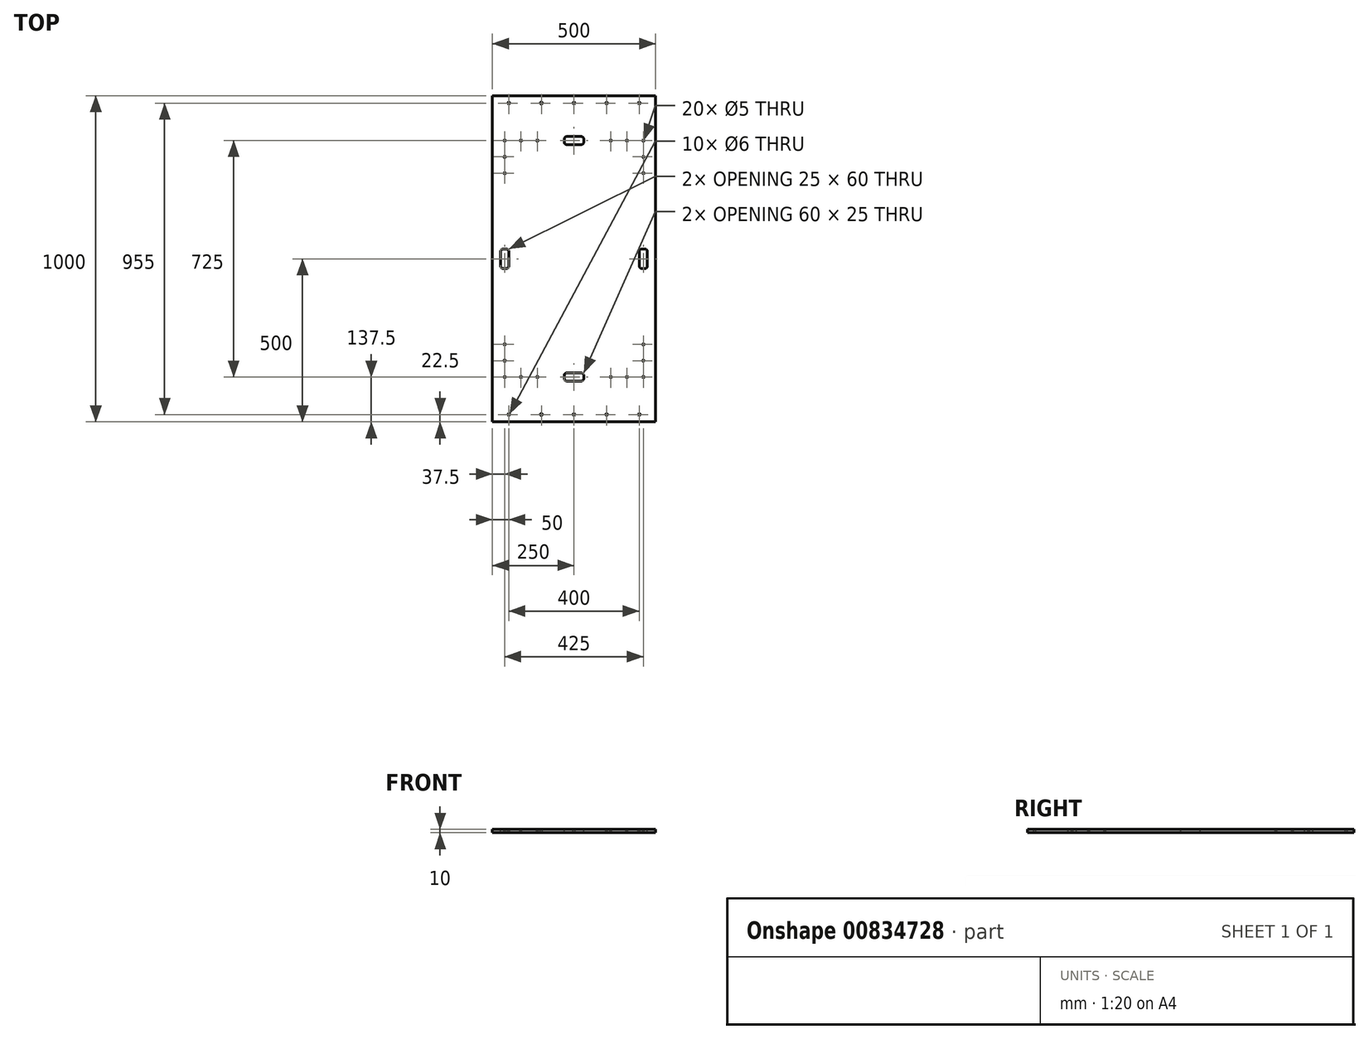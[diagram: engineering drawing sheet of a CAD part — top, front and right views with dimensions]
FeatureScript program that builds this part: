
annotation { "Feature Type Name" : "Feature", "Feature Type Description" : "" }
export const myFeature = defineFeature(function(context is Context, id is Id, definition is map)
    precondition{}
    {
        {
            var Q0;
            Q0=qCreatedBy(makeId("Top.planeOp"),FACE);
            var sketch = newSketch(context, id + "F0", { "sketchPlane" : qUnion([Q0])});
            skLineSegment(sketch, "E0.bottom", {"start": v(-250, 500) * mm, "end": v(250, 500) * mm});
            skLineSegment(sketch, "E0.top", {"start": v(-250, -500) * mm, "end": v(250, -500) * mm});
            skLineSegment(sketch, "E0.left", {"start": v(-250, 500) * mm, "end": v(-250, -500) * mm});
            skLineSegment(sketch, "E0.right", {"start": v(250, 500) * mm, "end": v(250, -500) * mm});
            skPoint(sketch, "E0.middle", {"position": v(0, 0) * mm});
            skSolve(sketch);
        }
        {
            var Q0;
            Q0=makeQuery(id+"F0.imprint","IMPRINT",FACE,{"disambiguationData":[TD([[makeQuery(id+"F0.imprint","IMPRINT",EDGE,{"derivedFrom":sQuery(id+"F0.wireOp",EDGE,"E0.bottom")}),-1.0]])]});
            extrude(context, id + "F1", {"entities" : qUnion([Q0]), "depth" : 10 * mm, "offsetDistance" : 25 * mm});
        }
        {
            var Q0;
            Q0=makeQuery(id+"F1.opExtrude","CAP_FACE",FACE,{"disambiguationData":[OSD([sQuery(id+"F0.wireOp",EDGE,"E0.bottom"),sQuery(id+"F0.wireOp",EDGE,"E0.top"),sQuery(id+"F0.wireOp",EDGE,"E0.left"),sQuery(id+"F0.wireOp",EDGE,"E0.right")])],"isStart":false});
            var sketch = newSketch(context, id + "F2", { "sketchPlane" : qUnion([Q0])});
            skLineSegment(sketch, "E1", {"start": v(250, 0) * mm, "end": v(-250, 0) * mm});
            skLineSegment(sketch, "E2", {"start": v(0, 500) * mm, "end": v(0, -500) * mm});
            skLineSegment(sketch, "E3", {"start": v(250, 477.5) * mm, "end": v(-250, 477.5) * mm});
            skLineSegment(sketch, "E4", {"start": v(250, -477.5) * mm, "end": v(-250, -477.5) * mm});
            skPoint(sketch, "E5", {"position": v(-200, 477.5) * mm});
            skPoint(sketch, "E6", {"position": v(-100, 477.5) * mm});
            skPoint(sketch, "E7", {"position": v(0, 477.5) * mm});
            skPoint(sketch, "E8", {"position": v(100, 477.5) * mm});
            skPoint(sketch, "E9", {"position": v(200, 477.5) * mm});
            skPoint(sketch, "E10", {"position": v(-200, -477.5) * mm});
            skPoint(sketch, "E11", {"position": v(-100, -477.5) * mm});
            skPoint(sketch, "E12", {"position": v(0, -477.5) * mm});
            skPoint(sketch, "E13", {"position": v(100, -477.5) * mm});
            skPoint(sketch, "E14", {"position": v(200, -477.5) * mm});
            skPoint(sketch, "E15", {"position": v(-212.5, 0) * mm});
            skPoint(sketch, "E16", {"position": v(212.5, 0) * mm});
            skLineSegment(sketch, "E17.bottom", {"start": v(200, -30) * mm, "end": v(225, -30) * mm});
            skLineSegment(sketch, "E17.top", {"start": v(200, 30) * mm, "end": v(225, 30) * mm});
            skLineSegment(sketch, "E17.left", {"start": v(200, -30) * mm, "end": v(200, 30) * mm});
            skLineSegment(sketch, "E17.right", {"start": v(225, -30) * mm, "end": v(225, 30) * mm});
            skLineSegment(sketch, "E18.bottom", {"start": v(-225, -30) * mm, "end": v(-200, -30) * mm});
            skLineSegment(sketch, "E18.top", {"start": v(-225, 30) * mm, "end": v(-200, 30) * mm});
            skLineSegment(sketch, "E18.left", {"start": v(-225, -30) * mm, "end": v(-225, 30) * mm});
            skLineSegment(sketch, "E18.right", {"start": v(-200, -30) * mm, "end": v(-200, 30) * mm});
            skSolve(sketch);
        }
        {
            var Q0;
            Q0=sQuery(id+"F2.wireOp",VERTEX,"E9");
            var Q1;
            Q1=sQuery(id+"F2.wireOp",VERTEX,"E8");
            var Q2;
            Q2=sQuery(id+"F2.wireOp",VERTEX,"E7");
            var Q3;
            Q3=sQuery(id+"F2.wireOp",VERTEX,"E6");
            var Q4;
            Q4=sQuery(id+"F2.wireOp",VERTEX,"E5");
            var Q5;
            Q5=sQuery(id+"F2.wireOp",VERTEX,"E14");
            var Q6;
            Q6=sQuery(id+"F2.wireOp",VERTEX,"E13");
            var Q7;
            Q7=sQuery(id+"F2.wireOp",VERTEX,"E12");
            var Q8;
            Q8=sQuery(id+"F2.wireOp",VERTEX,"E11");
            var Q9;
            Q9=sQuery(id+"F2.wireOp",VERTEX,"E10");
            var Q10;
            Q10=makeQuery(id+"F1.opExtrude","SWEPT_BODY",BODY,{"disambiguationData":[OSD([sQuery(id+"F0.wireOp",EDGE,"E0.bottom"),sQuery(id+"F0.wireOp",EDGE,"E0.top"),sQuery(id+"F0.wireOp",EDGE,"E0.left"),sQuery(id+"F0.wireOp",EDGE,"E0.right")])]});
            hole(context, id + "F3", {"style" : HoleStyle.SIMPLE, "endStyle" : HoleEndStyle.THROUGH, "holeDiameter" : 6 * mm, "majorDiameter" : 5 * mm, "isTappedThrough" : true, "tappedDepth" : 12 * mm, "tapClearance" : 3, "locations" : qUnion([Q0, Q1, Q2, Q3, Q4, Q5, Q6, Q7, Q8, Q9]), "scope" : qUnion([Q10])});
        }
        {
            var Q0;
            Q0 = qSketchRegion(id + "F2", true);
            extrude(context, id + "F4", {"entities" : qUnion([Q0]), "operationType" : NewBodyOperationType.REMOVE, "oppositeDirection" : true, "depth" : 25 * mm, "offsetDistance" : 25 * mm});
        }
        {
            var Q0;
            Q0=makeQuery(id+"F1.opExtrude","CAP_FACE",FACE,{"disambiguationData":[OSD([sQuery(id+"F0.wireOp",EDGE,"E0.bottom"),sQuery(id+"F0.wireOp",EDGE,"E0.top"),sQuery(id+"F0.wireOp",EDGE,"E0.left"),sQuery(id+"F0.wireOp",EDGE,"E0.right")])],"isStart":false});
            var sketch = newSketch(context, id + "F5", { "sketchPlane" : qUnion([Q0])});
            skLineSegment(sketch, "E19", {"start": v(0, -500) * mm, "end": v(0, 500) * mm});
            skPoint(sketch, "E20", {"position": v(0, -362.5) * mm});
            skPoint(sketch, "E21", {"position": v(0, 362.5) * mm});
            skLineSegment(sketch, "E22.bottom", {"start": v(30, 375) * mm, "end": v(-30, 375) * mm});
            skLineSegment(sketch, "E22.top", {"start": v(30, 350) * mm, "end": v(-30, 350) * mm});
            skLineSegment(sketch, "E22.left", {"start": v(30, 375) * mm, "end": v(30, 350) * mm});
            skLineSegment(sketch, "E22.right", {"start": v(-30, 375) * mm, "end": v(-30, 350) * mm});
            skLineSegment(sketch, "E23.bottom", {"start": v(30, -350) * mm, "end": v(-30, -350) * mm});
            skLineSegment(sketch, "E23.top", {"start": v(30, -375) * mm, "end": v(-30, -375) * mm});
            skLineSegment(sketch, "E23.left", {"start": v(30, -350) * mm, "end": v(30, -375) * mm});
            skLineSegment(sketch, "E23.right", {"start": v(-30, -350) * mm, "end": v(-30, -375) * mm});
            skPoint(sketch, "E24", {"position": v(0, 0) * mm});
            skSolve(sketch);
        }
        {
            var Q0;
            Q0 = qSketchRegion(id + "F5", true);
            extrude(context, id + "F6", {"entities" : qUnion([Q0]), "operationType" : NewBodyOperationType.REMOVE, "oppositeDirection" : true, "depth" : 25 * mm, "offsetDistance" : 25 * mm});
        }
        {
            var Q0;
            Q0=makeQuery(id+"F6.boolean.opBoolean","COPY",EDGE,{"derivedFrom":makeQuery(id+"F6.opExtrude","SWEPT_EDGE",EDGE,{"disambiguationData":[OSD([sQuery(id+"F5.wireOp",EDGE,"E22.bottom"),sQuery(id+"F5.wireOp",EDGE,"E22.left")])]})});
            var Q1;
            Q1=makeQuery(id+"F6.boolean.opBoolean","COPY",EDGE,{"derivedFrom":makeQuery(id+"F6.opExtrude","SWEPT_EDGE",EDGE,{"disambiguationData":[OSD([sQuery(id+"F5.wireOp",EDGE,"E22.top"),sQuery(id+"F5.wireOp",EDGE,"E22.left")])]})});
            var Q2;
            Q2=makeQuery(id+"F6.boolean.opBoolean","COPY",EDGE,{"derivedFrom":makeQuery(id+"F6.opExtrude","SWEPT_EDGE",EDGE,{"disambiguationData":[OSD([sQuery(id+"F5.wireOp",EDGE,"E22.bottom"),sQuery(id+"F5.wireOp",EDGE,"E22.right")])]})});
            var Q3;
            Q3=makeQuery(id+"F6.boolean.opBoolean","COPY",EDGE,{"derivedFrom":makeQuery(id+"F6.opExtrude","SWEPT_EDGE",EDGE,{"disambiguationData":[OSD([sQuery(id+"F5.wireOp",EDGE,"E22.top"),sQuery(id+"F5.wireOp",EDGE,"E22.right")])]})});
            var Q4;
            Q4=makeQuery(id+"F4.boolean.opBoolean","COPY",EDGE,{"derivedFrom":makeQuery(id+"F4.opExtrude","SWEPT_EDGE",EDGE,{"disambiguationData":[OSD([sQuery(id+"F2.wireOp",EDGE,"E17.bottom"),sQuery(id+"F2.wireOp",EDGE,"E17.left")])]})});
            var Q5;
            Q5=makeQuery(id+"F4.boolean.opBoolean","COPY",EDGE,{"derivedFrom":makeQuery(id+"F4.opExtrude","SWEPT_EDGE",EDGE,{"disambiguationData":[OSD([sQuery(id+"F2.wireOp",EDGE,"E17.top"),sQuery(id+"F2.wireOp",EDGE,"E17.right")])]})});
            var Q6;
            Q6=makeQuery(id+"F4.boolean.opBoolean","COPY",EDGE,{"derivedFrom":makeQuery(id+"F4.opExtrude","SWEPT_EDGE",EDGE,{"disambiguationData":[OSD([sQuery(id+"F2.wireOp",EDGE,"E17.top"),sQuery(id+"F2.wireOp",EDGE,"E17.left")])]})});
            var Q7;
            Q7=makeQuery(id+"F4.boolean.opBoolean","COPY",EDGE,{"derivedFrom":makeQuery(id+"F4.opExtrude","SWEPT_EDGE",EDGE,{"disambiguationData":[OSD([sQuery(id+"F2.wireOp",EDGE,"E17.bottom"),sQuery(id+"F2.wireOp",EDGE,"E17.right")])]})});
            var Q8;
            Q8=makeQuery(id+"F4.boolean.opBoolean","COPY",EDGE,{"derivedFrom":makeQuery(id+"F4.opExtrude","SWEPT_EDGE",EDGE,{"disambiguationData":[OSD([sQuery(id+"F2.wireOp",EDGE,"E18.bottom"),sQuery(id+"F2.wireOp",EDGE,"E18.right")])]})});
            var Q9;
            Q9=makeQuery(id+"F4.boolean.opBoolean","COPY",EDGE,{"derivedFrom":makeQuery(id+"F4.opExtrude","SWEPT_EDGE",EDGE,{"disambiguationData":[OSD([sQuery(id+"F2.wireOp",EDGE,"E18.top"),sQuery(id+"F2.wireOp",EDGE,"E18.right")])]})});
            var Q10;
            Q10=makeQuery(id+"F4.boolean.opBoolean","COPY",EDGE,{"derivedFrom":makeQuery(id+"F4.opExtrude","SWEPT_EDGE",EDGE,{"disambiguationData":[OSD([sQuery(id+"F2.wireOp",EDGE,"E18.top"),sQuery(id+"F2.wireOp",EDGE,"E18.left")])]})});
            var Q11;
            Q11=makeQuery(id+"F4.boolean.opBoolean","COPY",EDGE,{"derivedFrom":makeQuery(id+"F4.opExtrude","SWEPT_EDGE",EDGE,{"disambiguationData":[OSD([sQuery(id+"F2.wireOp",EDGE,"E18.bottom"),sQuery(id+"F2.wireOp",EDGE,"E18.left")])]})});
            var Q12;
            Q12=makeQuery(id+"F6.boolean.opBoolean","COPY",EDGE,{"derivedFrom":makeQuery(id+"F6.opExtrude","SWEPT_EDGE",EDGE,{"disambiguationData":[OSD([sQuery(id+"F5.wireOp",EDGE,"E23.top"),sQuery(id+"F5.wireOp",EDGE,"E23.right")])]})});
            var Q13;
            Q13=makeQuery(id+"F6.boolean.opBoolean","COPY",EDGE,{"derivedFrom":makeQuery(id+"F6.opExtrude","SWEPT_EDGE",EDGE,{"disambiguationData":[OSD([sQuery(id+"F5.wireOp",EDGE,"E23.top"),sQuery(id+"F5.wireOp",EDGE,"E23.left")])]})});
            var Q14;
            Q14=makeQuery(id+"F6.boolean.opBoolean","COPY",EDGE,{"derivedFrom":makeQuery(id+"F6.opExtrude","SWEPT_EDGE",EDGE,{"disambiguationData":[OSD([sQuery(id+"F5.wireOp",EDGE,"E23.bottom"),sQuery(id+"F5.wireOp",EDGE,"E23.left")])]})});
            var Q15;
            Q15=makeQuery(id+"F6.boolean.opBoolean","COPY",EDGE,{"derivedFrom":makeQuery(id+"F6.opExtrude","SWEPT_EDGE",EDGE,{"disambiguationData":[OSD([sQuery(id+"F5.wireOp",EDGE,"E23.bottom"),sQuery(id+"F5.wireOp",EDGE,"E23.right")])]})});
            fillet(context, id + "F7", {"entities" : qUnion([Q0, Q1, Q2, Q3, Q4, Q5, Q6, Q7, Q8, Q9, Q10, Q11, Q12, Q13, Q14, Q15]), "radius" : 8 * mm, "tangentPropagation" : true, "allowEdgeOverflow" : false});
        }
        {
            var Q0;
            Q0=makeQuery(id+"F1.opExtrude","CAP_FACE",FACE,{"disambiguationData":[OSD([sQuery(id+"F0.wireOp",EDGE,"E0.bottom"),sQuery(id+"F0.wireOp",EDGE,"E0.top"),sQuery(id+"F0.wireOp",EDGE,"E0.left"),sQuery(id+"F0.wireOp",EDGE,"E0.right")])],"isStart":false});
            var sketch = newSketch(context, id + "F8", { "sketchPlane" : qUnion([Q0])});
            skLineSegment(sketch, "E25.bottom", {"start": v(212.5, -362.5) * mm, "end": v(-212.5, -362.5) * mm});
            skLineSegment(sketch, "E25.top", {"start": v(212.5, 362.5) * mm, "end": v(-212.5, 362.5) * mm});
            skLineSegment(sketch, "E25.left", {"start": v(212.5, -362.5) * mm, "end": v(212.5, 362.5) * mm});
            skLineSegment(sketch, "E25.right", {"start": v(-212.5, -362.5) * mm, "end": v(-212.5, 362.5) * mm});
            skPoint(sketch, "E25.middle", {"position": v(0, 0) * mm});
            skPoint(sketch, "E26", {"position": v(-162.5, -362.5) * mm});
            skPoint(sketch, "E27", {"position": v(-112.5, -362.5) * mm});
            skPoint(sketch, "E28", {"position": v(-212.5, -312.5) * mm});
            skPoint(sketch, "E29", {"position": v(-212.5, -262.5) * mm});
            skPoint(sketch, "E30", {"position": v(212.5, -312.5) * mm});
            skPoint(sketch, "E31", {"position": v(162.5, -362.5) * mm});
            skPoint(sketch, "E32", {"position": v(212.5, -262.5) * mm});
            skPoint(sketch, "E33", {"position": v(112.5, -362.5) * mm});
            skPoint(sketch, "E34", {"position": v(112.5, 362.5) * mm});
            skPoint(sketch, "E35", {"position": v(162.5, 362.5) * mm});
            skPoint(sketch, "E36", {"position": v(212.5, 312.5) * mm});
            skPoint(sketch, "E37", {"position": v(212.5, 262.5) * mm});
            skPoint(sketch, "E38", {"position": v(-112.5, 362.5) * mm});
            skPoint(sketch, "E39", {"position": v(-162.5, 362.5) * mm});
            skPoint(sketch, "E40", {"position": v(-212.5, 312.5) * mm});
            skPoint(sketch, "E41", {"position": v(-212.5, 262.5) * mm});
            skSolve(sketch);
        }
        {
            var Q0;
            Q0=sQuery(id+"F8.wireOp",VERTEX,"E29");
            var Q1;
            Q1=sQuery(id+"F8.wireOp",VERTEX,"E28");
            var Q2;
            Q2=sQuery(id+"F8.wireOp",VERTEX,"E26");
            var Q3;
            Q3=sQuery(id+"F8.wireOp",VERTEX,"E27");
            var Q4;
            Q4=sQuery(id+"F8.wireOp",VERTEX,"E33");
            var Q5;
            Q5=sQuery(id+"F8.wireOp",VERTEX,"E31");
            var Q6;
            Q6=sQuery(id+"F8.wireOp",VERTEX,"E30");
            var Q7;
            Q7=sQuery(id+"F8.wireOp",VERTEX,"E32");
            var Q8;
            Q8=sQuery(id+"F8.wireOp",VERTEX,"E25.bottom.start");
            var Q9;
            Q9=sQuery(id+"F8.wireOp",VERTEX,"E25.bottom.end");
            var Q10;
            Q10=sQuery(id+"F8.wireOp",VERTEX,"E37");
            var Q11;
            Q11=sQuery(id+"F8.wireOp",VERTEX,"E36");
            var Q12;
            Q12=sQuery(id+"F8.wireOp",VERTEX,"E35");
            var Q13;
            Q13=sQuery(id+"F8.wireOp",VERTEX,"E34");
            var Q14;
            Q14=sQuery(id+"F8.wireOp",VERTEX,"E38");
            var Q15;
            Q15=sQuery(id+"F8.wireOp",VERTEX,"E39");
            var Q16;
            Q16=sQuery(id+"F8.wireOp",VERTEX,"E40");
            var Q17;
            Q17=sQuery(id+"F8.wireOp",VERTEX,"E41");
            var Q18;
            Q18=sQuery(id+"F8.wireOp",VERTEX,"E25.top.start");
            var Q19;
            Q19=sQuery(id+"F8.wireOp",VERTEX,"E25.top.end");
            var Q20;
            Q20=makeQuery(id+"F1.opExtrude","SWEPT_BODY",BODY,{"disambiguationData":[OSD([sQuery(id+"F0.wireOp",EDGE,"E0.bottom"),sQuery(id+"F0.wireOp",EDGE,"E0.top"),sQuery(id+"F0.wireOp",EDGE,"E0.left"),sQuery(id+"F0.wireOp",EDGE,"E0.right")])]});
            hole(context, id + "F9", {"style" : HoleStyle.SIMPLE, "endStyle" : HoleEndStyle.THROUGH, "holeDiameter" : 5 * mm, "majorDiameter" : 5 * mm, "isTappedThrough" : true, "tappedDepth" : 12 * mm, "tapClearance" : 3, "locations" : qUnion([Q0, Q1, Q2, Q3, Q4, Q5, Q6, Q7, Q8, Q9, Q10, Q11, Q12, Q13, Q14, Q15, Q16, Q17, Q18, Q19]), "scope" : qUnion([Q20])});
        }
    });
